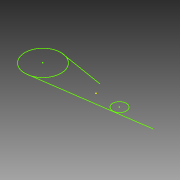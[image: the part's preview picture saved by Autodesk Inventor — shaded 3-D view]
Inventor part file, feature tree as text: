
AUTODESK INVENTOR PART (.ipt)
format: ipt  version: 2015 (Build 190159000, 159)  size: 57,344 bytes
history: native  units: mm
features: sketch x1
ambient origin geometry x8: Origin, YZ Plane, XZ Plane, XY Plane, X Axis, Y Axis, Z Axis, Center Point
feature tree (1):
  sketch  "Sketch1"
